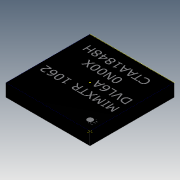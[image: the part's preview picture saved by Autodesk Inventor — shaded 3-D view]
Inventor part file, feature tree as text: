
AUTODESK INVENTOR PART (.ipt)
format: ipt  version: 2020 (Build 240168000, 168)  size: 143,872 bytes
history: native  units: in
note: dims shown in document units (in); Inventor stores cm internally (conversion verified against a paired STEP export)
features: other x2, sketch x1
ambient origin geometry x8: Origin, YZ Plane, XZ Plane, XY Plane, X Axis, Y Axis, Z Axis, Center Point
bodies: Solid1 (feature_tree)
feature tree (3):
  other  "Boss-Extrude1"
  sketch  "Sketch1"
  other  "Image2"
